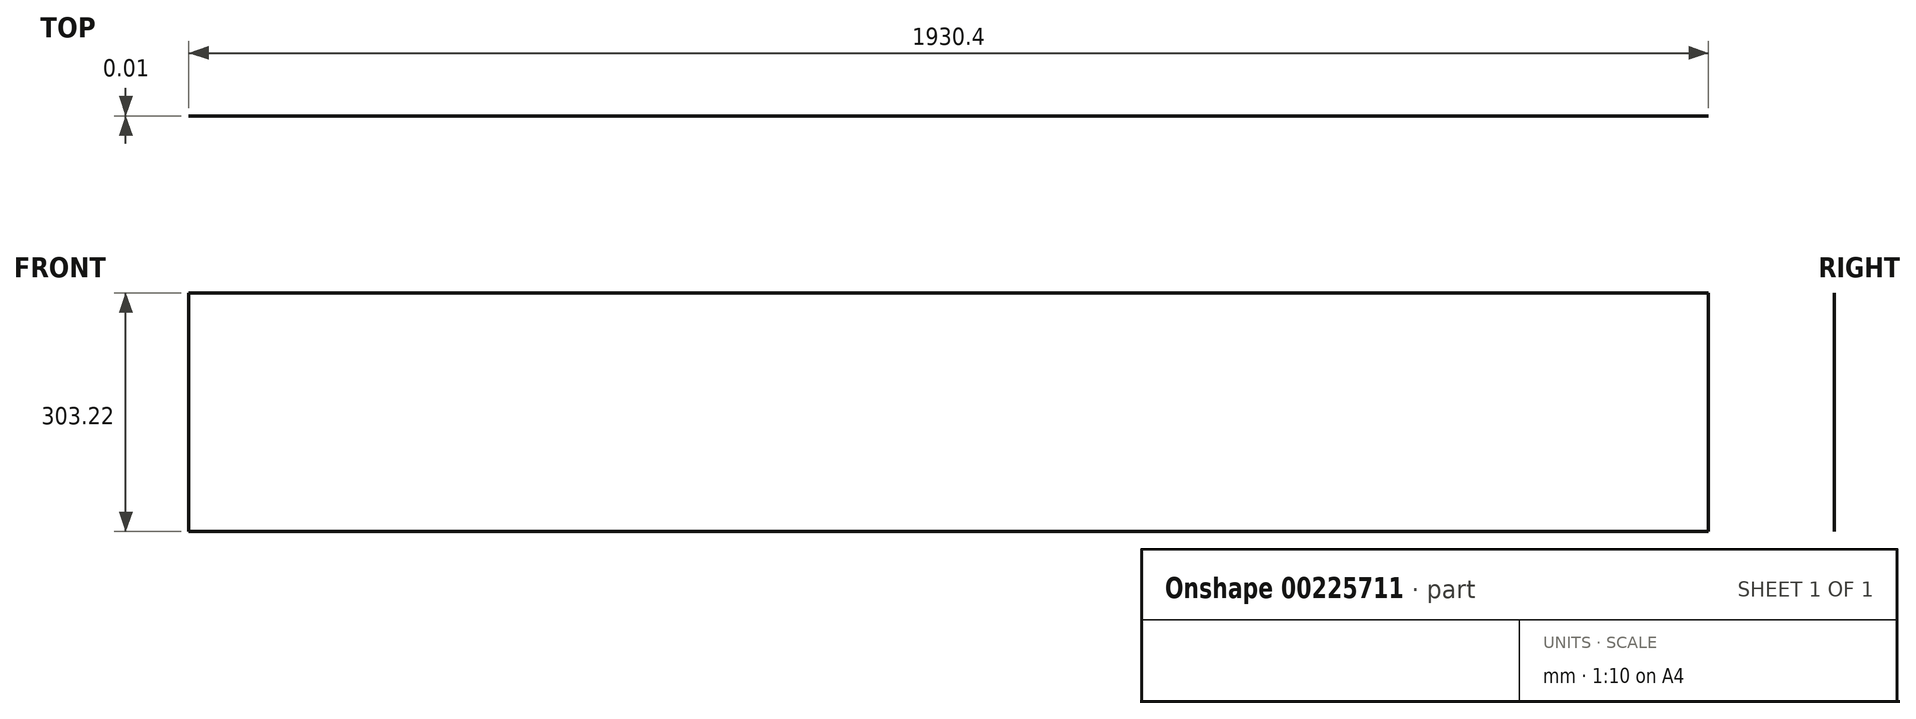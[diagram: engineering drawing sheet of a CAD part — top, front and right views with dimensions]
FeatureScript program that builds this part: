
annotation { "Feature Type Name" : "Feature", "Feature Type Description" : "" }
export const myFeature = defineFeature(function(context is Context, id is Id, definition is map)
    precondition{}
    {
        {
            var Q0;
            Q0=qCreatedBy(makeId("Front.planeOp"),FACE);
            var sketch = newSketch(context, id + "F0", { "sketchPlane" : qUnion([Q0])});
            skLineSegment(sketch, "E0.bottom", {"start": v(-113.73, 278.19) * mm, "end": v(1816.67, 278.19) * mm});
            skLineSegment(sketch, "E0.top", {"start": v(-113.73, -25.03) * mm, "end": v(1816.67, -25.03) * mm});
            skLineSegment(sketch, "E0.left", {"start": v(-113.73, 278.19) * mm, "end": v(-113.73, -25.03) * mm});
            skLineSegment(sketch, "E0.right", {"start": v(1816.67, 278.19) * mm, "end": v(1816.67, -25.03) * mm});
            skSolve(sketch);
        }
        {
            var Q0;
            Q0=makeQuery(id+"F0.imprint","IMPRINT",FACE,{"disambiguationData":[TD([[makeQuery(id+"F0.imprint","IMPRINT",EDGE,{"derivedFrom":sQuery(id+"F0.wireOp",EDGE,"E0.bottom")}),-1.0]])]});
            extrude(context, id + "F1", {"entities" : qUnion([Q0]), "depth" : 7 / 812.8 * mm});
        }
    });
